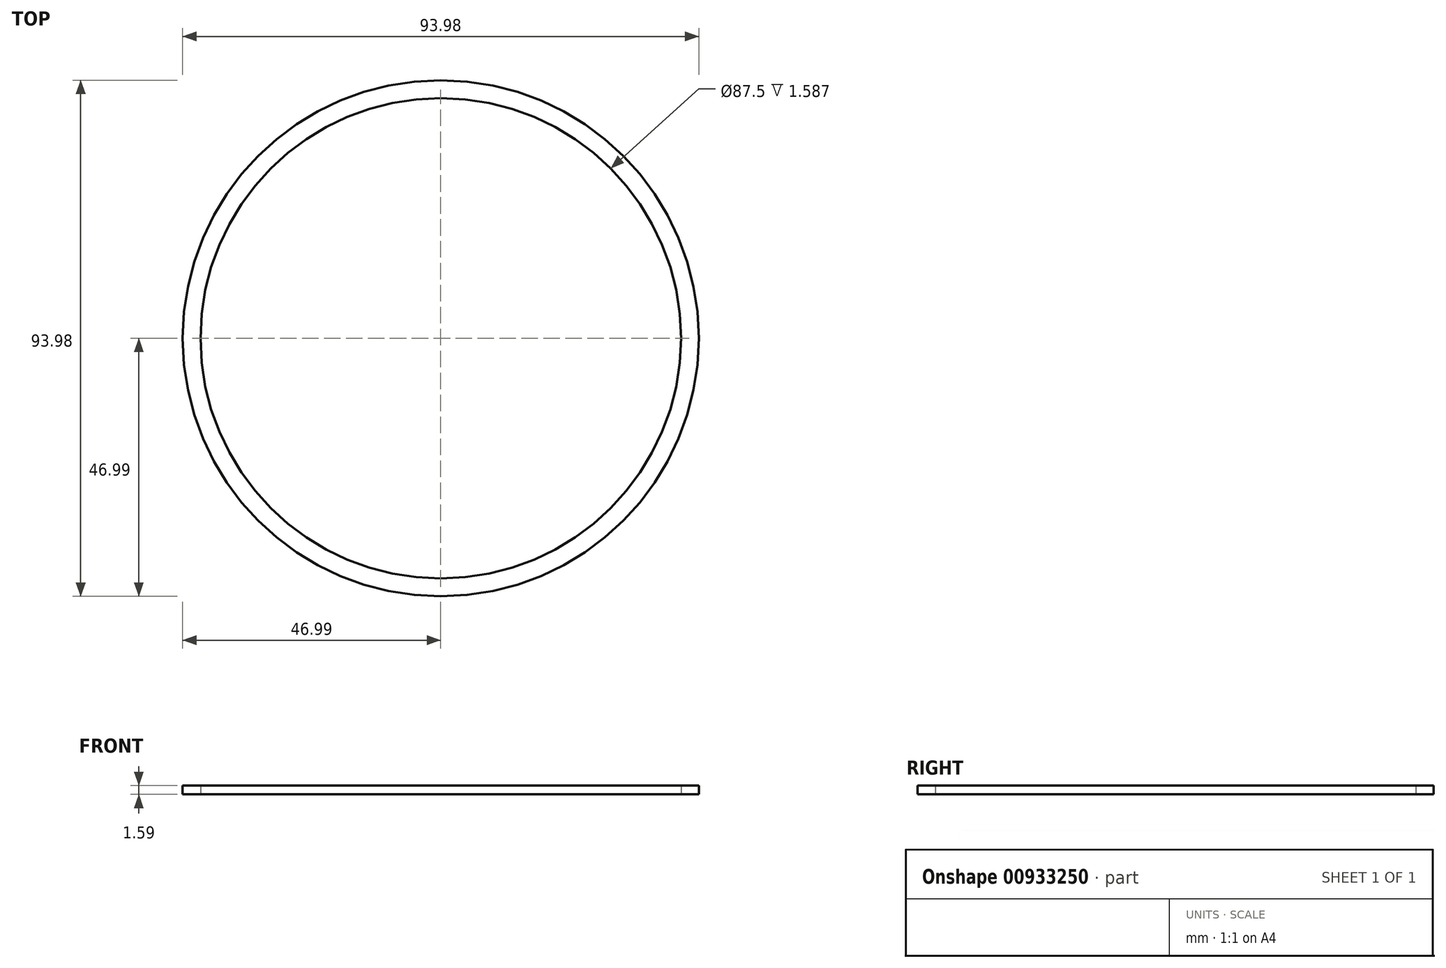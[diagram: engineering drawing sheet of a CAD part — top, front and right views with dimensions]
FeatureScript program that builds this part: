
annotation { "Feature Type Name" : "Feature", "Feature Type Description" : "" }
export const myFeature = defineFeature(function(context is Context, id is Id, definition is map)
    precondition{}
    {
        {
            var Q0;
            Q0=qCreatedBy(makeId("Top.planeOp"),FACE);
            var sketch = newSketch(context, id + "F0", { "sketchPlane" : qUnion([Q0])});
            skCircle(sketch, "E0", {"center": v(0, 0) * mm, "radius": 47 * mm});
            skCircle(sketch, "E1", {"center": v(0, 0) * mm, "radius": 43.75 * mm});
            skSolve(sketch);
        }
        {
            var Q0;
            Q0=qSketchRegion(id+"F0",true);
            extrude(context, id + "F1", {"entities" : qUnion([Q0]), "depth" : 1.59 * mm, "offsetDistance" : 25.4 * mm});
        }
    });
